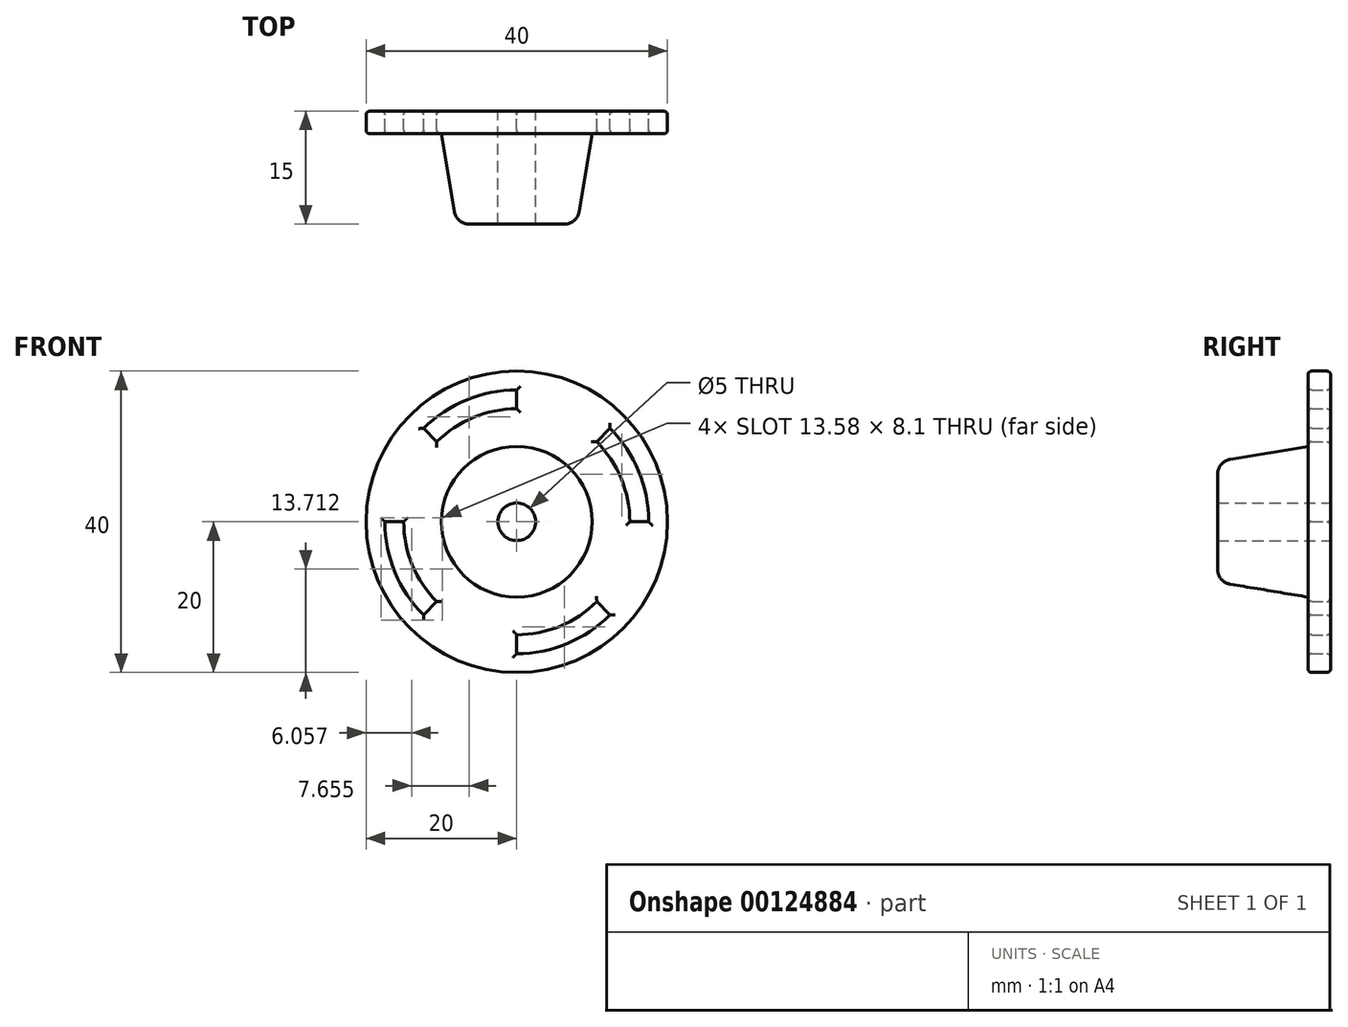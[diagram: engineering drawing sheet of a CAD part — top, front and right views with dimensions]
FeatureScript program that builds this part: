
annotation { "Feature Type Name" : "Feature", "Feature Type Description" : "" }
export const myFeature = defineFeature(function(context is Context, id is Id, definition is map)
    precondition{}
    {
        {
            var Q0;
            Q0=qCreatedBy(makeId("Front.planeOp"),FACE);
            var sketch = newSketch(context, id + "F0", { "sketchPlane" : qUnion([Q0])});
            skCircle(sketch, "E0", {"center": v(0, 0) * mm, "radius": 20 * mm});
            skCircle(sketch, "E1", {"center": v(0, 0) * mm, "radius": 10 * mm});
            skCircle(sketch, "E2", {"center": v(0, 0) * mm, "radius": 2.5 * mm});
            skCircle(sketch, "E3", {"center": v(0, 0) * mm, "radius": 17.5 * mm});
            skCircle(sketch, "E4", {"center": v(0, 0) * mm, "radius": 15 * mm});
            skLineSegment(sketch, "E5", {"start": v(0, 0) * mm, "end": v(0, 20) * mm});
            skLineSegment(sketch, "E6", {"start": v(0, 0) * mm, "end": v(20, 0) * mm});
            skLineSegment(sketch, "E7", {"start": v(0, 0) * mm, "end": v(0, -20) * mm});
            skLineSegment(sketch, "E8", {"start": v(0, 0) * mm, "end": v(-20, 0) * mm});
            skLineSegment(sketch, "E9", {"start": v(0, 0) * mm, "end": v(-14.14, 14.14) * mm});
            skLineSegment(sketch, "E10", {"start": v(0, 0) * mm, "end": v(14.14, 14.14) * mm});
            skLineSegment(sketch, "E11", {"start": v(0, 0) * mm, "end": v(14.14, -14.14) * mm});
            skLineSegment(sketch, "E12", {"start": v(0, 0) * mm, "end": v(-14.14, -14.14) * mm});
            skSolve(sketch);
        }
        {
            var Q0;
            {var subQ0=sQuery(id+"F0.wireOp",EDGE,"E8");var subQ1=sQuery(id+"F0.wireOp",EDGE,"E1");var subQ2=makeQuery(id+"F0.imprint","INTERSECT",VERTEX,{"derivedFrom":[subQ1,subQ0]});Q0=makeQuery(id+"F0.imprint","IMPRINT",FACE,{"disambiguationData":[TD([[makeQuery(id+"F0.imprint","IMPRINT",EDGE,{"disambiguationData":[TD([[subQ2,-1.0]])],"derivedFrom":subQ1}),1.0]])]});}
            var Q1;
            {var subQ0=sQuery(id+"F0.wireOp",EDGE,"E9");var subQ1=sQuery(id+"F0.wireOp",EDGE,"E1");var subQ2=makeQuery(id+"F0.imprint","INTERSECT",VERTEX,{"derivedFrom":[subQ1,subQ0]});Q1=makeQuery(id+"F0.imprint","IMPRINT",FACE,{"disambiguationData":[TD([[makeQuery(id+"F0.imprint","IMPRINT",EDGE,{"disambiguationData":[TD([[subQ2,-1.0]])],"derivedFrom":subQ1}),1.0]])]});}
            var Q2;
            {var subQ0=sQuery(id+"F0.wireOp",EDGE,"E5");var subQ1=sQuery(id+"F0.wireOp",EDGE,"E1");var subQ2=makeQuery(id+"F0.imprint","INTERSECT",VERTEX,{"derivedFrom":[subQ1,subQ0]});Q2=makeQuery(id+"F0.imprint","IMPRINT",FACE,{"disambiguationData":[TD([[makeQuery(id+"F0.imprint","IMPRINT",EDGE,{"disambiguationData":[TD([[subQ2,-1.0]])],"derivedFrom":subQ1}),1.0]])]});}
            var Q3;
            {var subQ0=sQuery(id+"F0.wireOp",EDGE,"E10");var subQ1=sQuery(id+"F0.wireOp",EDGE,"E1");var subQ2=makeQuery(id+"F0.imprint","INTERSECT",VERTEX,{"derivedFrom":[subQ1,subQ0]});Q3=makeQuery(id+"F0.imprint","IMPRINT",FACE,{"disambiguationData":[TD([[makeQuery(id+"F0.imprint","IMPRINT",EDGE,{"disambiguationData":[TD([[subQ2,-1.0]])],"derivedFrom":subQ1}),1.0]])]});}
            var Q4;
            {var subQ0=sQuery(id+"F0.wireOp",EDGE,"E10");var subQ1=sQuery(id+"F0.wireOp",EDGE,"E1");var subQ2=makeQuery(id+"F0.imprint","INTERSECT",VERTEX,{"derivedFrom":[subQ1,subQ0]});Q4=makeQuery(id+"F0.imprint","IMPRINT",FACE,{"disambiguationData":[TD([[makeQuery(id+"F0.imprint","IMPRINT",EDGE,{"disambiguationData":[TD([[subQ2,1.0]])],"derivedFrom":subQ1}),1.0]])]});}
            var Q5;
            {var subQ0=sQuery(id+"F0.wireOp",EDGE,"E6");var subQ1=sQuery(id+"F0.wireOp",EDGE,"E1");var subQ2=makeQuery(id+"F0.imprint","INTERSECT",VERTEX,{"derivedFrom":[subQ1,subQ0]});Q5=makeQuery(id+"F0.imprint","IMPRINT",FACE,{"disambiguationData":[TD([[makeQuery(id+"F0.imprint","IMPRINT",EDGE,{"disambiguationData":[TD([[subQ2,1.0]])],"derivedFrom":subQ1}),1.0]])]});}
            var Q6;
            {var subQ0=sQuery(id+"F0.wireOp",EDGE,"E7");var subQ1=sQuery(id+"F0.wireOp",EDGE,"E1");var subQ2=makeQuery(id+"F0.imprint","INTERSECT",VERTEX,{"derivedFrom":[subQ1,subQ0]});Q6=makeQuery(id+"F0.imprint","IMPRINT",FACE,{"disambiguationData":[TD([[makeQuery(id+"F0.imprint","IMPRINT",EDGE,{"disambiguationData":[TD([[subQ2,-1.0]])],"derivedFrom":subQ1}),1.0]])]});}
            var Q7;
            {var subQ0=sQuery(id+"F0.wireOp",EDGE,"E12");var subQ1=sQuery(id+"F0.wireOp",EDGE,"E1");var subQ2=makeQuery(id+"F0.imprint","INTERSECT",VERTEX,{"derivedFrom":[subQ1,subQ0]});Q7=makeQuery(id+"F0.imprint","IMPRINT",FACE,{"disambiguationData":[TD([[makeQuery(id+"F0.imprint","IMPRINT",EDGE,{"disambiguationData":[TD([[subQ2,-1.0]])],"derivedFrom":subQ1}),1.0]])]});}
            extrude(context, id + "F1", {"entities" : qUnion([Q0, Q1, Q2, Q3, Q4, Q5, Q6, Q7]), "depth" : 15 * mm});
        }
        {
            var Q0;
            {var subQ0=sQuery(id+"F0.wireOp",EDGE,"E8");var subQ1=sQuery(id+"F0.wireOp",EDGE,"E1");var subQ2=makeQuery(id+"F0.imprint","INTERSECT",VERTEX,{"derivedFrom":[subQ1,subQ0]});Q0=makeQuery(id+"F0.imprint","IMPRINT",FACE,{"disambiguationData":[TD([[makeQuery(id+"F0.imprint","IMPRINT",EDGE,{"disambiguationData":[TD([[subQ2,-1.0]])],"derivedFrom":subQ1}),-1.0]])]});}
            var Q1;
            {var subQ0=sQuery(id+"F0.wireOp",EDGE,"E8");var subQ1=sQuery(id+"F0.wireOp",EDGE,"E0");var subQ2=makeQuery(id+"F0.imprint","INTERSECT",VERTEX,{"derivedFrom":[subQ1,subQ0]});Q1=makeQuery(id+"F0.imprint","IMPRINT",FACE,{"disambiguationData":[TD([[makeQuery(id+"F0.imprint","IMPRINT",EDGE,{"disambiguationData":[TD([[subQ2,-1.0]])],"derivedFrom":subQ1}),1.0]])]});}
            var Q2;
            {var subQ0=sQuery(id+"F0.wireOp",EDGE,"E8");var subQ1=sQuery(id+"F0.wireOp",EDGE,"E0");var subQ2=makeQuery(id+"F0.imprint","INTERSECT",VERTEX,{"derivedFrom":[subQ1,subQ0]});Q2=makeQuery(id+"F0.imprint","IMPRINT",FACE,{"disambiguationData":[TD([[makeQuery(id+"F0.imprint","IMPRINT",EDGE,{"disambiguationData":[TD([[subQ2,1.0]])],"derivedFrom":subQ1}),1.0]])]});}
            var Q3;
            {var subQ0=sQuery(id+"F0.wireOp",EDGE,"E9");var subQ1=sQuery(id+"F0.wireOp",EDGE,"E3");var subQ2=makeQuery(id+"F0.imprint","INTERSECT",VERTEX,{"derivedFrom":[subQ1,subQ0]});Q3=makeQuery(id+"F0.imprint","IMPRINT",FACE,{"disambiguationData":[TD([[makeQuery(id+"F0.imprint","IMPRINT",EDGE,{"disambiguationData":[TD([[subQ2,-1.0]])],"derivedFrom":subQ1}),1.0]])]});}
            var Q4;
            {var subQ0=sQuery(id+"F0.wireOp",EDGE,"E9");var subQ1=sQuery(id+"F0.wireOp",EDGE,"E1");var subQ2=makeQuery(id+"F0.imprint","INTERSECT",VERTEX,{"derivedFrom":[subQ1,subQ0]});Q4=makeQuery(id+"F0.imprint","IMPRINT",FACE,{"disambiguationData":[TD([[makeQuery(id+"F0.imprint","IMPRINT",EDGE,{"disambiguationData":[TD([[subQ2,-1.0]])],"derivedFrom":subQ1}),-1.0]])]});}
            var Q5;
            {var subQ0=sQuery(id+"F0.wireOp",EDGE,"E12");var subQ1=sQuery(id+"F0.wireOp",EDGE,"E1");var subQ2=makeQuery(id+"F0.imprint","INTERSECT",VERTEX,{"derivedFrom":[subQ1,subQ0]});Q5=makeQuery(id+"F0.imprint","IMPRINT",FACE,{"disambiguationData":[TD([[makeQuery(id+"F0.imprint","IMPRINT",EDGE,{"disambiguationData":[TD([[subQ2,-1.0]])],"derivedFrom":subQ1}),-1.0]])]});}
            var Q6;
            {var subQ0=sQuery(id+"F0.wireOp",EDGE,"E12");var subQ1=sQuery(id+"F0.wireOp",EDGE,"E3");var subQ2=makeQuery(id+"F0.imprint","INTERSECT",VERTEX,{"derivedFrom":[subQ1,subQ0]});Q6=makeQuery(id+"F0.imprint","IMPRINT",FACE,{"disambiguationData":[TD([[makeQuery(id+"F0.imprint","IMPRINT",EDGE,{"disambiguationData":[TD([[subQ2,-1.0]])],"derivedFrom":subQ1}),1.0]])]});}
            var Q7;
            {var subQ0=sQuery(id+"F0.wireOp",EDGE,"E7");var subQ1=sQuery(id+"F0.wireOp",EDGE,"E0");var subQ2=makeQuery(id+"F0.imprint","INTERSECT",VERTEX,{"derivedFrom":[subQ1,subQ0]});Q7=makeQuery(id+"F0.imprint","IMPRINT",FACE,{"disambiguationData":[TD([[makeQuery(id+"F0.imprint","IMPRINT",EDGE,{"disambiguationData":[TD([[subQ2,1.0]])],"derivedFrom":subQ1}),1.0]])]});}
            var Q8;
            {var subQ0=sQuery(id+"F0.wireOp",EDGE,"E5");var subQ1=sQuery(id+"F0.wireOp",EDGE,"E1");var subQ2=makeQuery(id+"F0.imprint","INTERSECT",VERTEX,{"derivedFrom":[subQ1,subQ0]});Q8=makeQuery(id+"F0.imprint","IMPRINT",FACE,{"disambiguationData":[TD([[makeQuery(id+"F0.imprint","IMPRINT",EDGE,{"disambiguationData":[TD([[subQ2,-1.0]])],"derivedFrom":subQ1}),-1.0]])]});}
            var Q9;
            {var subQ0=sQuery(id+"F0.wireOp",EDGE,"E5");var subQ1=sQuery(id+"F0.wireOp",EDGE,"E0");var subQ2=makeQuery(id+"F0.imprint","INTERSECT",VERTEX,{"derivedFrom":[subQ1,subQ0]});Q9=makeQuery(id+"F0.imprint","IMPRINT",FACE,{"disambiguationData":[TD([[makeQuery(id+"F0.imprint","IMPRINT",EDGE,{"disambiguationData":[TD([[subQ2,-1.0]])],"derivedFrom":subQ1}),1.0]])]});}
            var Q10;
            {var subQ0=sQuery(id+"F0.wireOp",EDGE,"E5");var subQ1=sQuery(id+"F0.wireOp",EDGE,"E0");var subQ2=makeQuery(id+"F0.imprint","INTERSECT",VERTEX,{"derivedFrom":[subQ1,subQ0]});Q10=makeQuery(id+"F0.imprint","IMPRINT",FACE,{"disambiguationData":[TD([[makeQuery(id+"F0.imprint","IMPRINT",EDGE,{"disambiguationData":[TD([[subQ2,1.0]])],"derivedFrom":subQ1}),1.0]])]});}
            var Q11;
            {var subQ0=sQuery(id+"F0.wireOp",EDGE,"E10");var subQ1=sQuery(id+"F0.wireOp",EDGE,"E3");var subQ2=makeQuery(id+"F0.imprint","INTERSECT",VERTEX,{"derivedFrom":[subQ1,subQ0]});Q11=makeQuery(id+"F0.imprint","IMPRINT",FACE,{"disambiguationData":[TD([[makeQuery(id+"F0.imprint","IMPRINT",EDGE,{"disambiguationData":[TD([[subQ2,-1.0]])],"derivedFrom":subQ1}),1.0]])]});}
            var Q12;
            {var subQ0=sQuery(id+"F0.wireOp",EDGE,"E10");var subQ1=sQuery(id+"F0.wireOp",EDGE,"E1");var subQ2=makeQuery(id+"F0.imprint","INTERSECT",VERTEX,{"derivedFrom":[subQ1,subQ0]});Q12=makeQuery(id+"F0.imprint","IMPRINT",FACE,{"disambiguationData":[TD([[makeQuery(id+"F0.imprint","IMPRINT",EDGE,{"disambiguationData":[TD([[subQ2,-1.0]])],"derivedFrom":subQ1}),-1.0]])]});}
            var Q13;
            {var subQ0=sQuery(id+"F0.wireOp",EDGE,"E6");var subQ1=sQuery(id+"F0.wireOp",EDGE,"E0");var subQ2=makeQuery(id+"F0.imprint","INTERSECT",VERTEX,{"derivedFrom":[subQ1,subQ0]});Q13=makeQuery(id+"F0.imprint","IMPRINT",FACE,{"disambiguationData":[TD([[makeQuery(id+"F0.imprint","IMPRINT",EDGE,{"disambiguationData":[TD([[subQ2,-1.0]])],"derivedFrom":subQ1}),1.0]])]});}
            var Q14;
            {var subQ0=sQuery(id+"F0.wireOp",EDGE,"E10");var subQ1=sQuery(id+"F0.wireOp",EDGE,"E1");var subQ2=makeQuery(id+"F0.imprint","INTERSECT",VERTEX,{"derivedFrom":[subQ1,subQ0]});Q14=makeQuery(id+"F0.imprint","IMPRINT",FACE,{"disambiguationData":[TD([[makeQuery(id+"F0.imprint","IMPRINT",EDGE,{"disambiguationData":[TD([[subQ2,1.0]])],"derivedFrom":subQ1}),-1.0]])]});}
            var Q15;
            {var subQ0=sQuery(id+"F0.wireOp",EDGE,"E6");var subQ1=sQuery(id+"F0.wireOp",EDGE,"E0");var subQ2=makeQuery(id+"F0.imprint","INTERSECT",VERTEX,{"derivedFrom":[subQ1,subQ0]});Q15=makeQuery(id+"F0.imprint","IMPRINT",FACE,{"disambiguationData":[TD([[makeQuery(id+"F0.imprint","IMPRINT",EDGE,{"disambiguationData":[TD([[subQ2,1.0]])],"derivedFrom":subQ1}),1.0]])]});}
            var Q16;
            {var subQ0=sQuery(id+"F0.wireOp",EDGE,"E6");var subQ1=sQuery(id+"F0.wireOp",EDGE,"E3");var subQ2=makeQuery(id+"F0.imprint","INTERSECT",VERTEX,{"derivedFrom":[subQ1,subQ0]});Q16=makeQuery(id+"F0.imprint","IMPRINT",FACE,{"disambiguationData":[TD([[makeQuery(id+"F0.imprint","IMPRINT",EDGE,{"disambiguationData":[TD([[subQ2,1.0]])],"derivedFrom":subQ1}),1.0]])]});}
            var Q17;
            {var subQ0=sQuery(id+"F0.wireOp",EDGE,"E6");var subQ1=sQuery(id+"F0.wireOp",EDGE,"E1");var subQ2=makeQuery(id+"F0.imprint","INTERSECT",VERTEX,{"derivedFrom":[subQ1,subQ0]});Q17=makeQuery(id+"F0.imprint","IMPRINT",FACE,{"disambiguationData":[TD([[makeQuery(id+"F0.imprint","IMPRINT",EDGE,{"disambiguationData":[TD([[subQ2,1.0]])],"derivedFrom":subQ1}),-1.0]])]});}
            var Q18;
            {var subQ0=sQuery(id+"F0.wireOp",EDGE,"E7");var subQ1=sQuery(id+"F0.wireOp",EDGE,"E1");var subQ2=makeQuery(id+"F0.imprint","INTERSECT",VERTEX,{"derivedFrom":[subQ1,subQ0]});Q18=makeQuery(id+"F0.imprint","IMPRINT",FACE,{"disambiguationData":[TD([[makeQuery(id+"F0.imprint","IMPRINT",EDGE,{"disambiguationData":[TD([[subQ2,-1.0]])],"derivedFrom":subQ1}),-1.0]])]});}
            var Q19;
            {var subQ0=sQuery(id+"F0.wireOp",EDGE,"E7");var subQ1=sQuery(id+"F0.wireOp",EDGE,"E0");var subQ2=makeQuery(id+"F0.imprint","INTERSECT",VERTEX,{"derivedFrom":[subQ1,subQ0]});Q19=makeQuery(id+"F0.imprint","IMPRINT",FACE,{"disambiguationData":[TD([[makeQuery(id+"F0.imprint","IMPRINT",EDGE,{"disambiguationData":[TD([[subQ2,-1.0]])],"derivedFrom":subQ1}),1.0]])]});}
            extrude(context, id + "F2", {"entities" : qUnion([Q0, Q1, Q2, Q3, Q4, Q5, Q6, Q7, Q8, Q9, Q10, Q11, Q12, Q13, Q14, Q15, Q16, Q17, Q18, Q19]), "operationType" : NewBodyOperationType.ADD, "depth" : 3 * mm});
        }
        {
            var Q0;
            Q0=makeQuery(id+"F1.opExtrude","CAP_EDGE",EDGE,{"disambiguationData":[OSD([sQuery(id+"F0.wireOp",EDGE,"E1")])],"isStart":false});
            chamfer(context, id + "F3", {"entities" : qUnion([Q0]), "chamferType" : ChamferType.TWO_OFFSETS, "width1" : 2 * mm, "oppositeDirection" : false, "width2" : 12 * mm, "tangentPropagation" : true});
        }
        {
            var Q0;
            {var subQ0=sQuery(id+"F0.wireOp",EDGE,"E1");Q0=makeQuery(id+"F3.opChamfer","BLEND_EDGE",EDGE,{"blendedFrom":[makeQuery(id+"F1.opExtrude","CAP_EDGE",EDGE,{"disambiguationData":[OSD([subQ0])],"isStart":false}),makeQuery(id+"F1.opExtrude","CAP_FACE",FACE,{"disambiguationData":[OSD([subQ0,sQuery(id+"F0.wireOp",EDGE,"E2")])],"isStart":false})],"blendedInto":[makeQuery(id+"F1.opExtrude","CAP_FACE",FACE,{"disambiguationData":[OSD([subQ0,sQuery(id+"F0.wireOp",EDGE,"E2")])],"isStart":false})]});}
            fillet(context, id + "F4", {"entities" : qUnion([Q0]), "radius" : 2 * mm, "tangentPropagation" : true, "allowEdgeOverflow" : false});
        }
        {
            var Q0;
            Q0=makeQuery(id+"F2.opExtrude","CAP_EDGE",EDGE,{"disambiguationData":[OSD([sQuery(id+"F0.wireOp",EDGE,"E8")])],"isStart":false});
            var Q1;
            {var subQ0=sQuery(id+"F0.wireOp",EDGE,"E3");Q1=makeQuery(id+"F2.opExtrude","CAP_EDGE",EDGE,{"disambiguationData":[OSD([subQ0]),TDD([makeQuery(id+"F0.imprint","IMPRINT",EDGE,{"disambiguationData":[TD([[makeQuery(id+"F0.imprint","INTERSECT",VERTEX,{"derivedFrom":[subQ0,sQuery(id+"F0.wireOp",EDGE,"E8")]}),-1.0]])],"derivedFrom":subQ0})])],"isStart":false});}
            var Q2;
            {var subQ0=sQuery(id+"F0.wireOp",EDGE,"E4");Q2=makeQuery(id+"F2.opExtrude","CAP_EDGE",EDGE,{"disambiguationData":[OSD([subQ0]),TDD([makeQuery(id+"F0.imprint","IMPRINT",EDGE,{"disambiguationData":[TD([[makeQuery(id+"F0.imprint","INTERSECT",VERTEX,{"derivedFrom":[subQ0,sQuery(id+"F0.wireOp",EDGE,"E8")]}),-1.0]])],"derivedFrom":subQ0})])],"isStart":false});}
            var Q3;
            Q3=makeQuery(id+"F2.opExtrude","CAP_EDGE",EDGE,{"disambiguationData":[OSD([sQuery(id+"F0.wireOp",EDGE,"E12")])],"isStart":false});
            var Q4;
            {var subQ0=sQuery(id+"F0.wireOp",EDGE,"E4");Q4=makeQuery(id+"F2.opExtrude","CAP_EDGE",EDGE,{"disambiguationData":[OSD([subQ0]),TDD([makeQuery(id+"F0.imprint","IMPRINT",EDGE,{"disambiguationData":[TD([[makeQuery(id+"F0.imprint","INTERSECT",VERTEX,{"derivedFrom":[subQ0,sQuery(id+"F0.wireOp",EDGE,"E7")]}),-1.0]])],"derivedFrom":subQ0})])],"isStart":false});}
            var Q5;
            {var subQ0=sQuery(id+"F0.wireOp",EDGE,"E3");Q5=makeQuery(id+"F2.opExtrude","CAP_EDGE",EDGE,{"disambiguationData":[OSD([subQ0]),TDD([makeQuery(id+"F0.imprint","IMPRINT",EDGE,{"disambiguationData":[TD([[makeQuery(id+"F0.imprint","INTERSECT",VERTEX,{"derivedFrom":[subQ0,sQuery(id+"F0.wireOp",EDGE,"E7")]}),-1.0]])],"derivedFrom":subQ0})])],"isStart":false});}
            var Q6;
            Q6=makeQuery(id+"F2.opExtrude","CAP_EDGE",EDGE,{"disambiguationData":[OSD([sQuery(id+"F0.wireOp",EDGE,"E7")])],"isStart":false});
            var Q7;
            Q7=makeQuery(id+"F2.opExtrude","CAP_EDGE",EDGE,{"disambiguationData":[OSD([sQuery(id+"F0.wireOp",EDGE,"E11")])],"isStart":false});
            var Q8;
            Q8=makeQuery(id+"F2.opExtrude","CAP_EDGE",EDGE,{"disambiguationData":[OSD([sQuery(id+"F0.wireOp",EDGE,"E6")])],"isStart":false});
            var Q9;
            {var subQ0=sQuery(id+"F0.wireOp",EDGE,"E4");Q9=makeQuery(id+"F2.opExtrude","CAP_EDGE",EDGE,{"disambiguationData":[OSD([subQ0]),TDD([makeQuery(id+"F0.imprint","IMPRINT",EDGE,{"disambiguationData":[TD([[makeQuery(id+"F0.imprint","INTERSECT",VERTEX,{"derivedFrom":[subQ0,sQuery(id+"F0.wireOp",EDGE,"E10")]}),1.0]])],"derivedFrom":subQ0})])],"isStart":false});}
            var Q10;
            {var subQ0=sQuery(id+"F0.wireOp",EDGE,"E3");Q10=makeQuery(id+"F2.opExtrude","CAP_EDGE",EDGE,{"disambiguationData":[OSD([subQ0]),TDD([makeQuery(id+"F0.imprint","IMPRINT",EDGE,{"disambiguationData":[TD([[makeQuery(id+"F0.imprint","INTERSECT",VERTEX,{"derivedFrom":[subQ0,sQuery(id+"F0.wireOp",EDGE,"E10")]}),1.0]])],"derivedFrom":subQ0})])],"isStart":false});}
            var Q11;
            Q11=makeQuery(id+"F2.opExtrude","CAP_EDGE",EDGE,{"disambiguationData":[OSD([sQuery(id+"F0.wireOp",EDGE,"E10")])],"isStart":false});
            var Q12;
            Q12=makeQuery(id+"F2.opExtrude","CAP_EDGE",EDGE,{"disambiguationData":[OSD([sQuery(id+"F0.wireOp",EDGE,"E5")])],"isStart":false});
            var Q13;
            Q13=makeQuery(id+"F2.opExtrude","CAP_EDGE",EDGE,{"disambiguationData":[OSD([sQuery(id+"F0.wireOp",EDGE,"E9")])],"isStart":false});
            var Q14;
            {var subQ0=sQuery(id+"F0.wireOp",EDGE,"E3");Q14=makeQuery(id+"F2.opExtrude","CAP_EDGE",EDGE,{"disambiguationData":[OSD([subQ0]),TDD([makeQuery(id+"F0.imprint","IMPRINT",EDGE,{"disambiguationData":[TD([[makeQuery(id+"F0.imprint","INTERSECT",VERTEX,{"derivedFrom":[subQ0,sQuery(id+"F0.wireOp",EDGE,"E5")]}),-1.0]])],"derivedFrom":subQ0})])],"isStart":false});}
            var Q15;
            {var subQ0=sQuery(id+"F0.wireOp",EDGE,"E4");Q15=makeQuery(id+"F2.opExtrude","CAP_EDGE",EDGE,{"disambiguationData":[OSD([subQ0]),TDD([makeQuery(id+"F0.imprint","IMPRINT",EDGE,{"disambiguationData":[TD([[makeQuery(id+"F0.imprint","INTERSECT",VERTEX,{"derivedFrom":[subQ0,sQuery(id+"F0.wireOp",EDGE,"E5")]}),-1.0]])],"derivedFrom":subQ0})])],"isStart":false});}
            var Q16;
            {var subQ0=sQuery(id+"F0.wireOp",EDGE,"E4");Q16=makeQuery(id+"F2.opExtrude","CAP_EDGE",EDGE,{"disambiguationData":[OSD([subQ0]),TDD([makeQuery(id+"F0.imprint","IMPRINT",EDGE,{"disambiguationData":[TD([[makeQuery(id+"F0.imprint","INTERSECT",VERTEX,{"derivedFrom":[subQ0,sQuery(id+"F0.wireOp",EDGE,"E7")]}),-1.0]])],"derivedFrom":subQ0})])],"isStart":true});}
            var Q17;
            Q17=makeQuery(id+"F2.opExtrude","CAP_EDGE",EDGE,{"disambiguationData":[OSD([sQuery(id+"F0.wireOp",EDGE,"E7")])],"isStart":true});
            var Q18;
            {var subQ0=sQuery(id+"F0.wireOp",EDGE,"E3");Q18=makeQuery(id+"F2.opExtrude","CAP_EDGE",EDGE,{"disambiguationData":[OSD([subQ0]),TDD([makeQuery(id+"F0.imprint","IMPRINT",EDGE,{"disambiguationData":[TD([[makeQuery(id+"F0.imprint","INTERSECT",VERTEX,{"derivedFrom":[subQ0,sQuery(id+"F0.wireOp",EDGE,"E7")]}),-1.0]])],"derivedFrom":subQ0})])],"isStart":true});}
            var Q19;
            Q19=makeQuery(id+"F2.opExtrude","CAP_EDGE",EDGE,{"disambiguationData":[OSD([sQuery(id+"F0.wireOp",EDGE,"E11")])],"isStart":true});
            var Q20;
            Q20=makeQuery(id+"F2.opExtrude","CAP_EDGE",EDGE,{"disambiguationData":[OSD([sQuery(id+"F0.wireOp",EDGE,"E6")])],"isStart":true});
            var Q21;
            {var subQ0=sQuery(id+"F0.wireOp",EDGE,"E4");Q21=makeQuery(id+"F2.opExtrude","CAP_EDGE",EDGE,{"disambiguationData":[OSD([subQ0]),TDD([makeQuery(id+"F0.imprint","IMPRINT",EDGE,{"disambiguationData":[TD([[makeQuery(id+"F0.imprint","INTERSECT",VERTEX,{"derivedFrom":[subQ0,sQuery(id+"F0.wireOp",EDGE,"E10")]}),1.0]])],"derivedFrom":subQ0})])],"isStart":true});}
            var Q22;
            {var subQ0=sQuery(id+"F0.wireOp",EDGE,"E3");Q22=makeQuery(id+"F2.opExtrude","CAP_EDGE",EDGE,{"disambiguationData":[OSD([subQ0]),TDD([makeQuery(id+"F0.imprint","IMPRINT",EDGE,{"disambiguationData":[TD([[makeQuery(id+"F0.imprint","INTERSECT",VERTEX,{"derivedFrom":[subQ0,sQuery(id+"F0.wireOp",EDGE,"E10")]}),1.0]])],"derivedFrom":subQ0})])],"isStart":true});}
            var Q23;
            Q23=makeQuery(id+"F2.opExtrude","CAP_EDGE",EDGE,{"disambiguationData":[OSD([sQuery(id+"F0.wireOp",EDGE,"E10")])],"isStart":true});
            var Q24;
            Q24=makeQuery(id+"F2.opExtrude","CAP_EDGE",EDGE,{"disambiguationData":[OSD([sQuery(id+"F0.wireOp",EDGE,"E5")])],"isStart":true});
            var Q25;
            Q25=makeQuery(id+"F2.opExtrude","CAP_EDGE",EDGE,{"disambiguationData":[OSD([sQuery(id+"F0.wireOp",EDGE,"E9")])],"isStart":true});
            var Q26;
            {var subQ0=sQuery(id+"F0.wireOp",EDGE,"E3");Q26=makeQuery(id+"F2.opExtrude","CAP_EDGE",EDGE,{"disambiguationData":[OSD([subQ0]),TDD([makeQuery(id+"F0.imprint","IMPRINT",EDGE,{"disambiguationData":[TD([[makeQuery(id+"F0.imprint","INTERSECT",VERTEX,{"derivedFrom":[subQ0,sQuery(id+"F0.wireOp",EDGE,"E5")]}),-1.0]])],"derivedFrom":subQ0})])],"isStart":true});}
            var Q27;
            {var subQ0=sQuery(id+"F0.wireOp",EDGE,"E4");Q27=makeQuery(id+"F2.opExtrude","CAP_EDGE",EDGE,{"disambiguationData":[OSD([subQ0]),TDD([makeQuery(id+"F0.imprint","IMPRINT",EDGE,{"disambiguationData":[TD([[makeQuery(id+"F0.imprint","INTERSECT",VERTEX,{"derivedFrom":[subQ0,sQuery(id+"F0.wireOp",EDGE,"E5")]}),-1.0]])],"derivedFrom":subQ0})])],"isStart":true});}
            var Q28;
            Q28=makeQuery(id+"F2.opExtrude","CAP_EDGE",EDGE,{"disambiguationData":[OSD([sQuery(id+"F0.wireOp",EDGE,"E8")])],"isStart":true});
            var Q29;
            {var subQ0=sQuery(id+"F0.wireOp",EDGE,"E4");Q29=makeQuery(id+"F2.opExtrude","CAP_EDGE",EDGE,{"disambiguationData":[OSD([subQ0]),TDD([makeQuery(id+"F0.imprint","IMPRINT",EDGE,{"disambiguationData":[TD([[makeQuery(id+"F0.imprint","INTERSECT",VERTEX,{"derivedFrom":[subQ0,sQuery(id+"F0.wireOp",EDGE,"E8")]}),-1.0]])],"derivedFrom":subQ0})])],"isStart":true});}
            var Q30;
            {var subQ0=sQuery(id+"F0.wireOp",EDGE,"E3");Q30=makeQuery(id+"F2.opExtrude","CAP_EDGE",EDGE,{"disambiguationData":[OSD([subQ0]),TDD([makeQuery(id+"F0.imprint","IMPRINT",EDGE,{"disambiguationData":[TD([[makeQuery(id+"F0.imprint","INTERSECT",VERTEX,{"derivedFrom":[subQ0,sQuery(id+"F0.wireOp",EDGE,"E8")]}),-1.0]])],"derivedFrom":subQ0})])],"isStart":true});}
            var Q31;
            Q31=makeQuery(id+"F2.opExtrude","CAP_EDGE",EDGE,{"disambiguationData":[OSD([sQuery(id+"F0.wireOp",EDGE,"E12")])],"isStart":true});
            var Q32;
            Q32=makeQuery(id+"F2.opExtrude","CAP_EDGE",EDGE,{"disambiguationData":[OSD([sQuery(id+"F0.wireOp",EDGE,"E0")])],"isStart":false});
            var Q33;
            Q33=makeQuery(id+"F2.opExtrude","CAP_EDGE",EDGE,{"disambiguationData":[OSD([sQuery(id+"F0.wireOp",EDGE,"E0")])],"isStart":true});
            fillet(context, id + "F5", {"entities" : qUnion([Q0, Q1, Q2, Q3, Q4, Q5, Q6, Q7, Q8, Q9, Q10, Q11, Q12, Q13, Q14, Q15, Q16, Q17, Q18, Q19, Q20, Q21, Q22, Q23, Q24, Q25, Q26, Q27, Q28, Q29, Q30, Q31, Q32, Q33]), "radius" : 0.5 * mm, "tangentPropagation" : true, "allowEdgeOverflow" : false});
        }
    });
